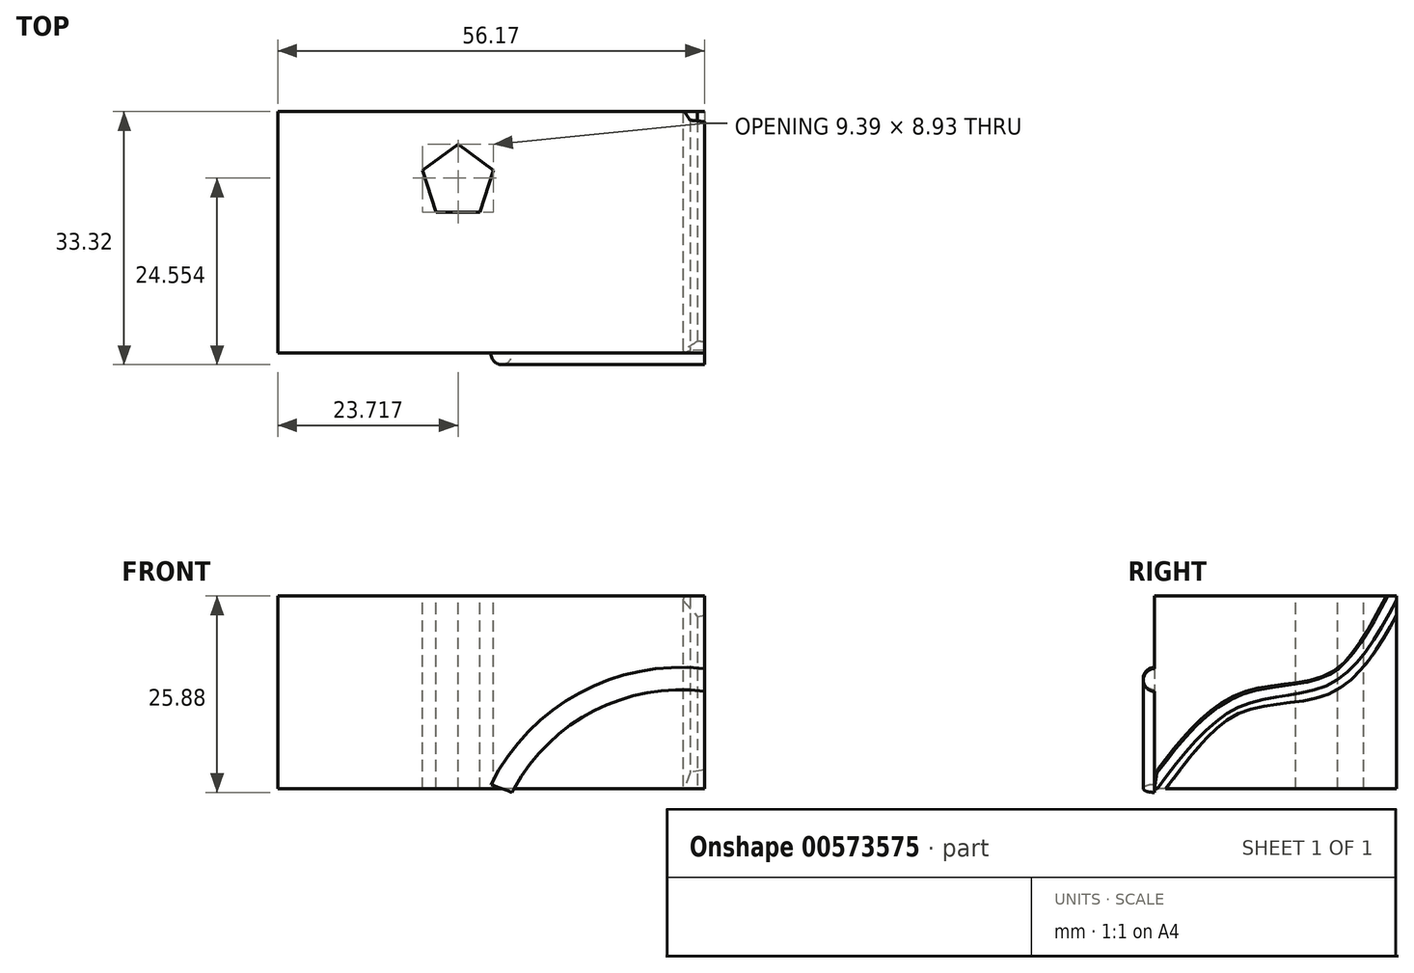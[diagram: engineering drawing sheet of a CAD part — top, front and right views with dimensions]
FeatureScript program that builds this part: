
annotation { "Feature Type Name" : "Feature", "Feature Type Description" : "" }
export const myFeature = defineFeature(function(context is Context, id is Id, definition is map)
    precondition{}
    {
        {
            var Q0;
            Q0=qCreatedBy(makeId("Top.planeOp"),FACE);
            var sketch = newSketch(context, id + "F0", { "sketchPlane" : qUnion([Q0])});
            skLineSegment(sketch, "E0.bottom", {"start": v(0, 0) * mm, "end": v(-56.17, 0) * mm});
            skLineSegment(sketch, "E0.top", {"start": v(0, 31.83) * mm, "end": v(-56.17, 31.83) * mm});
            skLineSegment(sketch, "E0.left", {"start": v(0, 0) * mm, "end": v(0, 31.83) * mm});
            skLineSegment(sketch, "E0.right", {"start": v(-56.17, 0) * mm, "end": v(-56.17, 31.83) * mm});
            skSolve(sketch);
        }
        {
            var Q0;
            Q0=makeQuery(id+"F0.imprint","IMPRINT",FACE,{"disambiguationData":[TD([[makeQuery(id+"F0.imprint","IMPRINT",EDGE,{"derivedFrom":sQuery(id+"F0.wireOp",EDGE,"E0.bottom")}),-1.0]])]});
            extrude(context, id + "F1", {"entities" : qUnion([Q0]), "depth" : 25.4 * mm, "offsetDistance" : 25.4 * mm});
        }
        {
            var Q0;
            Q0=makeQuery(id+"F1.opExtrude","CAP_FACE",FACE,{"disambiguationData":[OSD([sQuery(id+"F0.wireOp",EDGE,"E0.bottom"),sQuery(id+"F0.wireOp",EDGE,"E0.top"),sQuery(id+"F0.wireOp",EDGE,"E0.left"),sQuery(id+"F0.wireOp",EDGE,"E0.right")])],"isStart":false});
            var sketch = newSketch(context, id + "F2", { "sketchPlane" : qUnion([Q0])});
            skCircle(sketch, "E1.cCircle", {"center": v(-32.45, 22.6) * mm, "radius": 4 * mm, "construction": true});
            skLineSegment(sketch, "E1.0", {"start": v(-29.55, 18.6) * mm, "end": v(-35.36, 18.6) * mm});
            skLineSegment(sketch, "E1.1", {"start": v(-35.36, 18.6) * mm, "end": v(-37.15, 24.12) * mm});
            skLineSegment(sketch, "E1.2", {"start": v(-37.15, 24.12) * mm, "end": v(-32.45, 27.53) * mm});
            skLineSegment(sketch, "E1.3", {"start": v(-32.45, 27.53) * mm, "end": v(-27.76, 24.12) * mm});
            skLineSegment(sketch, "E1.4", {"start": v(-27.76, 24.12) * mm, "end": v(-29.55, 18.6) * mm});
            skPoint(sketch, "E1.0.midPoint", {"position": v(-32.45, 18.6) * mm});
            skSolve(sketch);
        }
        {
            var Q0;
            Q0=makeQuery(id+"F2.imprint","IMPRINT",FACE,{"disambiguationData":[TD([[makeQuery(id+"F2.imprint","IMPRINT",EDGE,{"derivedFrom":sQuery(id+"F2.wireOp",EDGE,"E1.0")}),-1.0]])]});
            extrude(context, id + "F3", {"entities" : qUnion([Q0]), "operationType" : NewBodyOperationType.REMOVE, "oppositeDirection" : true, "depth" : 45.2 * mm, "offsetDistance" : 25.4 * mm});
        }
        {
            var Q0;
            Q0=makeQuery(id+"F1.opExtrude","SWEPT_FACE",FACE,{"disambiguationData":[OSD([sQuery(id+"F0.wireOp",EDGE,"E0.bottom")])]});
            var sketch = newSketch(context, id + "F4", { "sketchPlane" : qUnion([Q0])});
            skArc(sketch, "E2", {"start": v(0, 14.22) * mm, "mid": v(-15.55, 11.3) * mm, "end": v(-26.62, 0) * mm});
            skSolve(sketch);
        }
        {
            var Q0;
            Q0=makeQuery(id+"F1.opExtrude","SWEPT_FACE",FACE,{"disambiguationData":[OSD([sQuery(id+"F0.wireOp",EDGE,"E0.left")])]});
            var sketch = newSketch(context, id + "F5", { "sketchPlane" : qUnion([Q0])});
            skCircle(sketch, "E3", {"center": v(0, 14.33) * mm, "radius": 1.5 * mm});
            skSolve(sketch);
        }
        {
            var Q0;
            {var subQ0=sQuery(id+"F5.wireOp",EDGE,"E3");var subQ1=makeQuery(id+"F1.opExtrude","SWEPT_EDGE",EDGE,{"disambiguationData":[OSD([sQuery(id+"F0.wireOp",EDGE,"E0.bottom"),sQuery(id+"F0.wireOp",EDGE,"E0.left")])]});var subQ2=makeQuery(id+"F5.imprint","INTERSECT",VERTEX,{"disambiguationData":[OD(0.0)],"derivedFrom":[subQ1,subQ0]});Q0=makeQuery(id+"F5.imprint","IMPRINT",FACE,{"disambiguationData":[TD([[makeQuery(id+"F5.imprint","IMPRINT",EDGE,{"disambiguationData":[TD([[subQ2,1.0]])],"derivedFrom":subQ0}),1.0]])]});}
            var Q1;
            Q1=sQuery(id+"F4.wireOp",EDGE,"E2");
            sweep(context, id + "F6", {"operationType" : NewBodyOperationType.ADD, "profiles" : qUnion([Q0]), "path" : qUnion([Q1])});
        }
        {
            var Q0;
            {var subQ0=sQuery(id+"F0.wireOp",EDGE,"E0.left");Q0=makeQuery(id+"F6.boolean.opBoolean","MERGE",FACE,{"derivedFrom":[makeQuery(id+"F1.opExtrude","SWEPT_FACE",FACE,{"disambiguationData":[OSD([subQ0])]}),makeQuery(id+"F6.opSweep","CAP_FACE",FACE,{"disambiguationData":[OSD([sQuery(id+"F0.wireOp",EDGE,"E0.bottom"),subQ0,sQuery(id+"F4.wireOp",VERTEX,"E2.start"),sQuery(id+"F5.wireOp",EDGE,"E3")])],"isStart":true})]});}
            var sketch = newSketch(context, id + "F7", { "sketchPlane" : qUnion([Q0])});
            skFitSpline(sketch, "E4", {"points": [v(0, 0) * mm, v(11.24, 11.1) * mm, v(23.17, 14.18) * mm, v(31.83, 25.4) * mm], "startDerivative": vector(29.16, 39.12) * mm, "endDerivative": vector(22.06, 41.42) * mm});
            skSolve(sketch);
        }
        {
            var Q0;
            Q0=makeQuery(id+"F1.opExtrude","SWEPT_FACE",FACE,{"disambiguationData":[OSD([sQuery(id+"F0.wireOp",EDGE,"E0.top")])]});
            var sketch = newSketch(context, id + "F8", { "sketchPlane" : qUnion([Q0])});
            skCircle(sketch, "E5.cCircle", {"center": v(0, 25.4) * mm, "radius": 2.5 * mm, "construction": true});
            skLineSegment(sketch, "E5.0", {"start": v(2.82, 24.82) * mm, "end": v(0.9, 22.67) * mm});
            skLineSegment(sketch, "E5.1", {"start": v(0.9, 22.67) * mm, "end": v(-1.91, 23.25) * mm});
            skLineSegment(sketch, "E5.2", {"start": v(-1.91, 23.25) * mm, "end": v(-2.82, 25.98) * mm});
            skLineSegment(sketch, "E5.3", {"start": v(-2.82, 25.98) * mm, "end": v(-0.9, 28.13) * mm});
            skLineSegment(sketch, "E5.4", {"start": v(-0.9, 28.13) * mm, "end": v(1.91, 27.55) * mm});
            skLineSegment(sketch, "E5.5", {"start": v(1.91, 27.55) * mm, "end": v(2.82, 24.82) * mm});
            skPoint(sketch, "E5.0.midPoint", {"position": v(1.86, 23.74) * mm});
            skSolve(sketch);
        }
        {
            var Q0;
            {var subQ1=sQuery(id+"F8.wireOp",EDGE,"E5.2");Q0=makeQuery(id+"F8.imprint","IMPRINT",FACE,{"disambiguationData":[TD([[makeQuery(id+"F8.imprint","IMPRINT",EDGE,{"derivedFrom":subQ1}),-1.0]])]});}
            var Q1;
            {var subQ1=sQuery(id+"F8.wireOp",EDGE,"E5.0");Q1=makeQuery(id+"F8.imprint","IMPRINT",FACE,{"disambiguationData":[TD([[makeQuery(id+"F8.imprint","IMPRINT",EDGE,{"derivedFrom":subQ1}),-1.0]])]});}
            var Q2;
            Q2=sQuery(id+"F7.wireOp",EDGE,"E4");
            sweep(context, id + "F9", {"operationType" : NewBodyOperationType.REMOVE, "profiles" : qUnion([Q0, Q1]), "path" : qUnion([Q2])});
        }
    });
